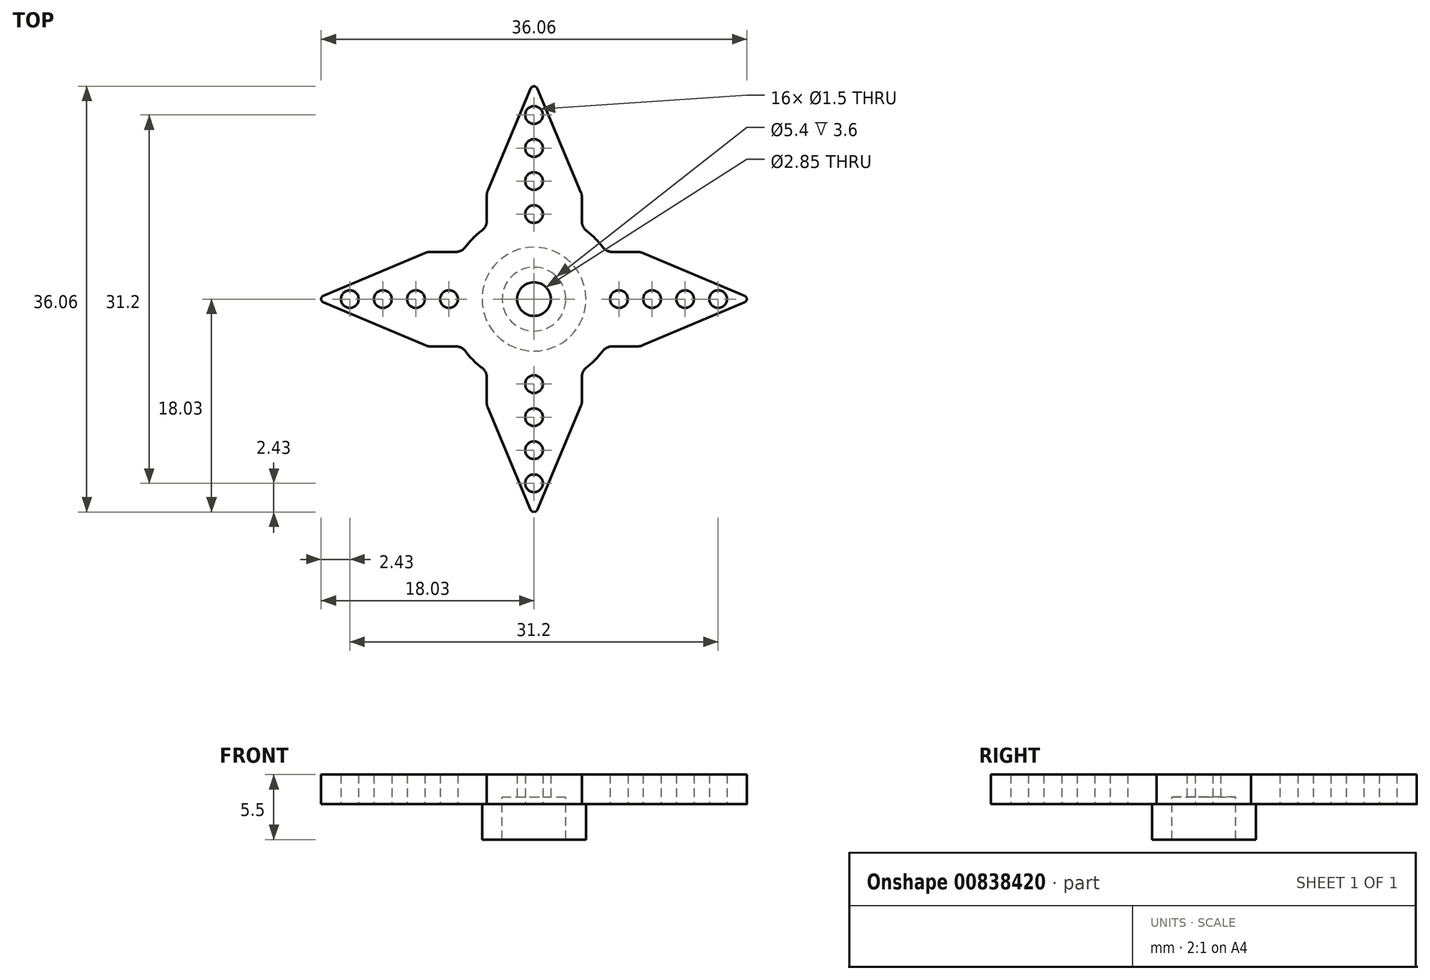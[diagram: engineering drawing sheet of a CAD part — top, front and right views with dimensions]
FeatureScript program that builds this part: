
annotation { "Feature Type Name" : "Feature", "Feature Type Description" : "" }
export const myFeature = defineFeature(function(context is Context, id is Id, definition is map)
    precondition{}
    {
        {
            var Q0;
            Q0=qCreatedBy(makeId("Top.planeOp"),FACE);
            var sketch = newSketch(context, id + "F0", { "sketchPlane" : qUnion([Q0])});
            skCircle(sketch, "E0", {"center": v(0, 0) * mm, "radius": 18.5 * mm, "construction": true});
            skArc(sketch, "E1", {"start": v(5.83, 4.4) * mm, "mid": v(5.18, 5.14) * mm, "end": v(4.45, 5.8) * mm});
            skLineSegment(sketch, "E2", {"start": v(-0.28, 17.84) * mm, "end": v(-3.92, 9.19) * mm});
            skLineSegment(sketch, "E3", {"start": v(-4, 6.62) * mm, "end": v(-4, 8.8) * mm});
            skLineSegment(sketch, "E4", {"start": v(0.28, 17.84) * mm, "end": v(3.98, 9.06) * mm});
            skLineSegment(sketch, "E5", {"start": v(4.05, 8.67) * mm, "end": v(4.05, 6.58) * mm});
            skLineSegment(sketch, "E6.1.0", {"start": v(-8.8, 4) * mm, "end": v(-6.62, 4) * mm});
            skLineSegment(sketch, "E6.1.4", {"start": v(-17.84, 0.28) * mm, "end": v(-9.19, 3.92) * mm});
            skLineSegment(sketch, "E6.3.2", {"start": v(6.62, 4) * mm, "end": v(8.8, 4) * mm});
            skLineSegment(sketch, "E6.3.3", {"start": v(17.84, 0.28) * mm, "end": v(9.19, 3.92) * mm});
            skArc(sketch, "E7.trimOffspring", {"start": v(-4.4, 5.83) * mm, "mid": v(-5.16, 5.16) * mm, "end": v(-5.83, 4.4) * mm});
            skPoint(sketch, "E8.orphan", {"position": v(5, 4) * mm});
            skPoint(sketch, "E9.orphan", {"position": v(4.05, 4.48) * mm});
            skPoint(sketch, "E10.orphan", {"position": v(-4, 5) * mm});
            skPoint(sketch, "E11.orphan", {"position": v(4, -5) * mm});
            skPoint(sketch, "E12.orphan", {"position": v(4.75, -4) * mm});
            skPoint(sketch, "E13.orphan", {"position": v(-4, -4.75) * mm});
            skPoint(sketch, "E14.orphan", {"position": v(-5, -4) * mm});
            skPoint(sketch, "E15.orphan", {"position": v(-4.75, 4) * mm});
            skPoint(sketch, "E16.visualSharp", {"position": v(4.05, 8.87) * mm});
            skArc(sketch, "E16.filletArc", {"start": v(4.05, 8.67) * mm, "mid": v(4.04, 8.87) * mm, "end": v(3.98, 9.06) * mm});
            skPoint(sketch, "E17.visualSharp", {"position": v(-4, 9) * mm});
            skArc(sketch, "E17.filletArc", {"start": v(-3.92, 9.19) * mm, "mid": v(-3.98, 9) * mm, "end": v(-4, 8.8) * mm});
            skPoint(sketch, "E18.visualSharp", {"position": v(4.05, 6.07) * mm});
            skArc(sketch, "E18.filletArc", {"start": v(4.05, 6.58) * mm, "mid": v(4.16, 6.14) * mm, "end": v(4.45, 5.8) * mm});
            skPoint(sketch, "E19.visualSharp", {"position": v(6.1, 4) * mm});
            skArc(sketch, "E19.filletArc", {"start": v(5.83, 4.4) * mm, "mid": v(6.18, 4.1) * mm, "end": v(6.62, 4) * mm});
            skPoint(sketch, "E20.visualSharp", {"position": v(9, 4) * mm});
            skArc(sketch, "E20.filletArc", {"start": v(9.19, 3.92) * mm, "mid": v(9, 3.98) * mm, "end": v(8.8, 4) * mm});
            skPoint(sketch, "E21.visualSharp", {"position": v(-6.1, 4) * mm});
            skArc(sketch, "E21.filletArc", {"start": v(-6.62, 4) * mm, "mid": v(-6.18, 4.1) * mm, "end": v(-5.83, 4.4) * mm});
            skPoint(sketch, "E22.visualSharp", {"position": v(-4, 6.1) * mm});
            skArc(sketch, "E22.filletArc", {"start": v(-4.4, 5.83) * mm, "mid": v(-4.1, 6.18) * mm, "end": v(-4, 6.62) * mm});
            skPoint(sketch, "E23.visualSharp", {"position": v(-9, 4) * mm});
            skArc(sketch, "E23.filletArc", {"start": v(-8.8, 4) * mm, "mid": v(-9, 3.98) * mm, "end": v(-9.19, 3.92) * mm});
            skLineSegment(sketch, "E24.MirrorCS", {"start": v(17.84, -0.28) * mm, "end": v(9.19, -3.92) * mm});
            skArc(sketch, "E25.MirrorCS", {"start": v(-3.92, -9.19) * mm, "mid": v(-3.98, -9) * mm, "end": v(-4, -8.8) * mm});
            skArc(sketch, "E26.MirrorCS", {"start": v(4.05, -8.67) * mm, "mid": v(4.04, -8.87) * mm, "end": v(3.98, -9.06) * mm});
            skArc(sketch, "E27.MirrorCS", {"start": v(-4.4, -5.83) * mm, "mid": v(-4.1, -6.18) * mm, "end": v(-4, -6.62) * mm});
            skLineSegment(sketch, "E28.MirrorCS", {"start": v(4.05, -8.67) * mm, "end": v(4.05, -6.58) * mm});
            skLineSegment(sketch, "E29.MirrorCS", {"start": v(-4, -6.62) * mm, "end": v(-4, -8.8) * mm});
            skArc(sketch, "E30.MirrorCS", {"start": v(-6.62, -4) * mm, "mid": v(-6.18, -4.1) * mm, "end": v(-5.83, -4.4) * mm});
            skArc(sketch, "E31.MirrorCS", {"start": v(4.05, -6.58) * mm, "mid": v(4.16, -6.14) * mm, "end": v(4.45, -5.8) * mm});
            skArc(sketch, "E32.MirrorCS", {"start": v(5.83, -4.4) * mm, "mid": v(5.18, -5.14) * mm, "end": v(4.45, -5.8) * mm});
            skArc(sketch, "E33.MirrorCS", {"start": v(9.19, -3.92) * mm, "mid": v(9, -3.98) * mm, "end": v(8.8, -4) * mm});
            skLineSegment(sketch, "E34.MirrorCS", {"start": v(-8.8, -4) * mm, "end": v(-6.62, -4) * mm});
            skArc(sketch, "E35.MirrorCS", {"start": v(-8.8, -4) * mm, "mid": v(-9, -3.98) * mm, "end": v(-9.19, -3.92) * mm});
            skArc(sketch, "E36.MirrorCS", {"start": v(5.83, -4.4) * mm, "mid": v(6.18, -4.1) * mm, "end": v(6.62, -4) * mm});
            skArc(sketch, "E37.MirrorCS", {"start": v(-4.4, -5.83) * mm, "mid": v(-5.16, -5.16) * mm, "end": v(-5.83, -4.4) * mm});
            skLineSegment(sketch, "E38.MirrorCS", {"start": v(6.62, -4) * mm, "end": v(8.8, -4) * mm});
            skPoint(sketch, "E39.MirrorP", {"position": v(-4, -6.1) * mm});
            skPoint(sketch, "E40.MirrorP", {"position": v(-4.75, -4) * mm});
            skPoint(sketch, "E41.MirrorP", {"position": v(5, -4) * mm});
            skPoint(sketch, "E42.MirrorP", {"position": v(4.05, -8.87) * mm});
            skPoint(sketch, "E43.MirrorP", {"position": v(6.1, -4) * mm});
            skPoint(sketch, "E44.MirrorP", {"position": v(4.05, -6.07) * mm});
            skPoint(sketch, "E45.MirrorP", {"position": v(-6.1, -4) * mm});
            skPoint(sketch, "E46.MirrorP", {"position": v(-9, -4) * mm});
            skPoint(sketch, "E47.MirrorP", {"position": v(4.05, -4.48) * mm});
            skPoint(sketch, "E48.MirrorP", {"position": v(-4, -5) * mm});
            skLineSegment(sketch, "E49.MirrorCS", {"start": v(-17.84, -0.28) * mm, "end": v(-9.19, -3.92) * mm});
            skLineSegment(sketch, "E50.MirrorCS", {"start": v(-0.28, -17.84) * mm, "end": v(-3.92, -9.19) * mm});
            skPoint(sketch, "E51.MirrorP", {"position": v(-4, -9) * mm});
            skLineSegment(sketch, "E52.MirrorCS", {"start": v(0.28, -17.84) * mm, "end": v(3.98, -9.06) * mm});
            skPoint(sketch, "E53.MirrorP", {"position": v(9, -4) * mm});
            skPoint(sketch, "E54.visualSharp", {"position": v(0, 18.5) * mm});
            skArc(sketch, "E54.filletArc", {"start": v(0.28, 17.84) * mm, "mid": v(0, 18.03) * mm, "end": v(-0.28, 17.84) * mm});
            skPoint(sketch, "E55.visualSharp", {"position": v(-18.5, 0) * mm});
            skPoint(sketch, "E56.visualSharp", {"position": v(18.5, 0) * mm});
            skArc(sketch, "E56.filletArc", {"start": v(17.84, -0.28) * mm, "mid": v(18.03, 0) * mm, "end": v(17.84, 0.28) * mm});
            skPoint(sketch, "E57.visualSharp", {"position": v(0, -18.5) * mm});
            skArc(sketch, "E57.filletArc", {"start": v(-0.28, -17.84) * mm, "mid": v(0, -18.03) * mm, "end": v(0.28, -17.84) * mm});
            skArc(sketch, "E58.filletArc", {"start": v(-17.84, 0.28) * mm, "mid": v(-18.03, 0) * mm, "end": v(-17.84, -0.28) * mm});
            skCircle(sketch, "E59", {"center": v(0, 0) * mm, "radius": 7.2 * mm, "construction": true});
            skCircle(sketch, "E60", {"center": v(7.2, 0) * mm, "radius": 0.75 * mm});
            skCircle(sketch, "E61.1.0.0", {"center": v(10, 0) * mm, "radius": 0.75 * mm});
            skCircle(sketch, "E61.2.0.0", {"center": v(12.8, 0) * mm, "radius": 0.75 * mm});
            skCircle(sketch, "E61.3.0.0", {"center": v(15.6, 0) * mm, "radius": 0.75 * mm});
            skLineSegment(sketch, "E61.direction1", {"start": v(7.2, 0) * mm, "end": v(10, 0) * mm, "construction": true});
            skCircle(sketch, "E62.1.0", {"center": v(0, 7.2) * mm, "radius": 0.75 * mm});
            skCircle(sketch, "E62.1.1", {"center": v(0, 12.8) * mm, "radius": 0.75 * mm});
            skCircle(sketch, "E62.1.2", {"center": v(0, 15.6) * mm, "radius": 0.75 * mm});
            skCircle(sketch, "E62.1.3", {"center": v(0, 10) * mm, "radius": 0.75 * mm});
            skCircle(sketch, "E62.2.0", {"center": v(-7.2, 0) * mm, "radius": 0.75 * mm});
            skCircle(sketch, "E62.2.1", {"center": v(-12.8, 0) * mm, "radius": 0.75 * mm});
            skCircle(sketch, "E62.2.2", {"center": v(-15.6, 0) * mm, "radius": 0.75 * mm});
            skCircle(sketch, "E62.2.3", {"center": v(-10, 0) * mm, "radius": 0.75 * mm});
            skCircle(sketch, "E62.3.0", {"center": v(0, -7.2) * mm, "radius": 0.75 * mm});
            skCircle(sketch, "E62.3.1", {"center": v(0, -12.8) * mm, "radius": 0.75 * mm});
            skCircle(sketch, "E62.3.2", {"center": v(0, -15.6) * mm, "radius": 0.75 * mm});
            skCircle(sketch, "E62.3.3", {"center": v(0, -10) * mm, "radius": 0.75 * mm});
            skSolve(sketch);
        }
        {
            var Q0;
            Q0 = qSketchRegion(id + "F0", true);
            extrude(context, id + "F1", {"entities" : qUnion([Q0]), "depth" : 2.5 * mm, "offsetDistance" : 25 * mm});
        }
        {
            var Q0;
            Q0=makeQuery(id+"F1.opExtrude","CAP_FACE",FACE,{"disambiguationData":[OSD([sQuery(id+"F0.wireOp",EDGE,"E1"),sQuery(id+"F0.wireOp",EDGE,"E2"),sQuery(id+"F0.wireOp",EDGE,"E3"),sQuery(id+"F0.wireOp",EDGE,"E4"),sQuery(id+"F0.wireOp",EDGE,"E5"),sQuery(id+"F0.wireOp",EDGE,"E6.1.0"),sQuery(id+"F0.wireOp",EDGE,"E6.1.4"),sQuery(id+"F0.wireOp",EDGE,"E6.3.2"),sQuery(id+"F0.wireOp",EDGE,"E6.3.3"),sQuery(id+"F0.wireOp",EDGE,"E7.trimOffspring"),sQuery(id+"F0.wireOp",EDGE,"E16.filletArc"),sQuery(id+"F0.wireOp",EDGE,"E18.filletArc"),sQuery(id+"F0.wireOp",EDGE,"E19.filletArc"),sQuery(id+"F0.wireOp",EDGE,"E20.filletArc"),sQuery(id+"F0.wireOp",EDGE,"E21.filletArc"),sQuery(id+"F0.wireOp",EDGE,"E22.filletArc"),sQuery(id+"F0.wireOp",EDGE,"E17.filletArc"),sQuery(id+"F0.wireOp",EDGE,"E23.filletArc"),sQuery(id+"F0.wireOp",EDGE,"E24.MirrorCS"),sQuery(id+"F0.wireOp",EDGE,"E26.MirrorCS"),sQuery(id+"F0.wireOp",EDGE,"E25.MirrorCS"),sQuery(id+"F0.wireOp",EDGE,"E27.MirrorCS"),sQuery(id+"F0.wireOp",EDGE,"E28.MirrorCS"),sQuery(id+"F0.wireOp",EDGE,"E29.MirrorCS"),sQuery(id+"F0.wireOp",EDGE,"E30.MirrorCS"),sQuery(id+"F0.wireOp",EDGE,"E31.MirrorCS"),sQuery(id+"F0.wireOp",EDGE,"E32.MirrorCS"),sQuery(id+"F0.wireOp",EDGE,"E33.MirrorCS"),sQuery(id+"F0.wireOp",EDGE,"E34.MirrorCS"),sQuery(id+"F0.wireOp",EDGE,"E35.MirrorCS"),sQuery(id+"F0.wireOp",EDGE,"E36.MirrorCS"),sQuery(id+"F0.wireOp",EDGE,"E37.MirrorCS"),sQuery(id+"F0.wireOp",EDGE,"E38.MirrorCS"),sQuery(id+"F0.wireOp",EDGE,"E49.MirrorCS"),sQuery(id+"F0.wireOp",EDGE,"E50.MirrorCS"),sQuery(id+"F0.wireOp",EDGE,"E52.MirrorCS"),sQuery(id+"F0.wireOp",EDGE,"E54.filletArc"),sQuery(id+"F0.wireOp",EDGE,"E56.filletArc"),sQuery(id+"F0.wireOp",EDGE,"E57.filletArc"),sQuery(id+"F0.wireOp",EDGE,"E58.filletArc"),sQuery(id+"F0.wireOp",EDGE,"E60"),sQuery(id+"F0.wireOp",EDGE,"E61.1.0.0"),sQuery(id+"F0.wireOp",EDGE,"E61.2.0.0"),sQuery(id+"F0.wireOp",EDGE,"E61.3.0.0"),sQuery(id+"F0.wireOp",EDGE,"E62.1.0"),sQuery(id+"F0.wireOp",EDGE,"E62.1.1"),sQuery(id+"F0.wireOp",EDGE,"E62.1.2"),sQuery(id+"F0.wireOp",EDGE,"E62.1.3"),sQuery(id+"F0.wireOp",EDGE,"E62.2.0"),sQuery(id+"F0.wireOp",EDGE,"E62.2.1"),sQuery(id+"F0.wireOp",EDGE,"E62.2.2"),sQuery(id+"F0.wireOp",EDGE,"E62.2.3"),sQuery(id+"F0.wireOp",EDGE,"E62.3.0"),sQuery(id+"F0.wireOp",EDGE,"E62.3.1"),sQuery(id+"F0.wireOp",EDGE,"E62.3.2"),sQuery(id+"F0.wireOp",EDGE,"E62.3.3")])],"isStart":true});
            var sketch = newSketch(context, id + "F2", { "sketchPlane" : qUnion([Q0])});
            skCircle(sketch, "E63", {"center": v(0, 0) * mm, "radius": 4.4 * mm});
            skCircle(sketch, "E64", {"center": v(0, 0) * mm, "radius": 2.7 * mm});
            skSolve(sketch);
        }
        {
            var Q0;
            Q0=makeQuery(id+"F2.imprint","IMPRINT",FACE,{"disambiguationData":[TD([[makeQuery(id+"F2.imprint","IMPRINT",EDGE,{"derivedFrom":sQuery(id+"F2.wireOp",EDGE,"E63")}),1.0]])]});
            var Q1;
            Q1=sQuery(id+"F2.wireOp",EDGE,"E63");
            var Q2;
            Q2=sQuery(id+"F2.wireOp",EDGE,"E64");
            extrude(context, id + "F3", {"entities" : qUnion([Q0]), "operationType" : NewBodyOperationType.ADD, "surfaceEntities" : qUnion([Q1, Q2]), "depth" : 3 * mm, "offsetDistance" : 25 * mm});
        }
        {
            var Q0;
            Q0=makeQuery(id+"F3.boolean.opBoolean","SPLIT",FACE,{"disambiguationData":[TD([makeQuery(id+"F3.opExtrude","SWEPT_FACE",FACE,{"disambiguationData":[OSD([sQuery(id+"F2.wireOp",EDGE,"E64")])]})])],"derivedFrom":makeQuery(id+"F1.opExtrude","CAP_FACE",FACE,{"disambiguationData":[OSD([sQuery(id+"F0.wireOp",EDGE,"E1"),sQuery(id+"F0.wireOp",EDGE,"E2"),sQuery(id+"F0.wireOp",EDGE,"E3"),sQuery(id+"F0.wireOp",EDGE,"E4"),sQuery(id+"F0.wireOp",EDGE,"E5"),sQuery(id+"F0.wireOp",EDGE,"E6.1.0"),sQuery(id+"F0.wireOp",EDGE,"E6.1.4"),sQuery(id+"F0.wireOp",EDGE,"E6.3.2"),sQuery(id+"F0.wireOp",EDGE,"E6.3.3"),sQuery(id+"F0.wireOp",EDGE,"E7.trimOffspring"),sQuery(id+"F0.wireOp",EDGE,"E16.filletArc"),sQuery(id+"F0.wireOp",EDGE,"E18.filletArc"),sQuery(id+"F0.wireOp",EDGE,"E19.filletArc"),sQuery(id+"F0.wireOp",EDGE,"E20.filletArc"),sQuery(id+"F0.wireOp",EDGE,"E21.filletArc"),sQuery(id+"F0.wireOp",EDGE,"E22.filletArc"),sQuery(id+"F0.wireOp",EDGE,"E17.filletArc"),sQuery(id+"F0.wireOp",EDGE,"E23.filletArc"),sQuery(id+"F0.wireOp",EDGE,"E24.MirrorCS"),sQuery(id+"F0.wireOp",EDGE,"E26.MirrorCS"),sQuery(id+"F0.wireOp",EDGE,"E25.MirrorCS"),sQuery(id+"F0.wireOp",EDGE,"E27.MirrorCS"),sQuery(id+"F0.wireOp",EDGE,"E28.MirrorCS"),sQuery(id+"F0.wireOp",EDGE,"E29.MirrorCS"),sQuery(id+"F0.wireOp",EDGE,"E30.MirrorCS"),sQuery(id+"F0.wireOp",EDGE,"E31.MirrorCS"),sQuery(id+"F0.wireOp",EDGE,"E32.MirrorCS"),sQuery(id+"F0.wireOp",EDGE,"E33.MirrorCS"),sQuery(id+"F0.wireOp",EDGE,"E34.MirrorCS"),sQuery(id+"F0.wireOp",EDGE,"E35.MirrorCS"),sQuery(id+"F0.wireOp",EDGE,"E36.MirrorCS"),sQuery(id+"F0.wireOp",EDGE,"E37.MirrorCS"),sQuery(id+"F0.wireOp",EDGE,"E38.MirrorCS"),sQuery(id+"F0.wireOp",EDGE,"E49.MirrorCS"),sQuery(id+"F0.wireOp",EDGE,"E50.MirrorCS"),sQuery(id+"F0.wireOp",EDGE,"E52.MirrorCS"),sQuery(id+"F0.wireOp",EDGE,"E54.filletArc"),sQuery(id+"F0.wireOp",EDGE,"E56.filletArc"),sQuery(id+"F0.wireOp",EDGE,"E57.filletArc"),sQuery(id+"F0.wireOp",EDGE,"E58.filletArc"),sQuery(id+"F0.wireOp",EDGE,"E60"),sQuery(id+"F0.wireOp",EDGE,"E61.1.0.0"),sQuery(id+"F0.wireOp",EDGE,"E61.2.0.0"),sQuery(id+"F0.wireOp",EDGE,"E61.3.0.0"),sQuery(id+"F0.wireOp",EDGE,"E62.1.0"),sQuery(id+"F0.wireOp",EDGE,"E62.1.1"),sQuery(id+"F0.wireOp",EDGE,"E62.1.2"),sQuery(id+"F0.wireOp",EDGE,"E62.1.3"),sQuery(id+"F0.wireOp",EDGE,"E62.2.0"),sQuery(id+"F0.wireOp",EDGE,"E62.2.1"),sQuery(id+"F0.wireOp",EDGE,"E62.2.2"),sQuery(id+"F0.wireOp",EDGE,"E62.2.3"),sQuery(id+"F0.wireOp",EDGE,"E62.3.0"),sQuery(id+"F0.wireOp",EDGE,"E62.3.1"),sQuery(id+"F0.wireOp",EDGE,"E62.3.2"),sQuery(id+"F0.wireOp",EDGE,"E62.3.3")])],"isStart":true})});
            var sketch = newSketch(context, id + "F4", { "sketchPlane" : qUnion([Q0])});
            skCircle(sketch, "E65", {"center": v(0, 0) * mm, "radius": 1.43 * mm});
            skSolve(sketch);
        }
        {
            var Q0;
            Q0=makeQuery(id+"F4.imprint","IMPRINT",FACE,{"disambiguationData":[TD([[makeQuery(id+"F4.imprint","IMPRINT",EDGE,{"derivedFrom":sQuery(id+"F4.wireOp",EDGE,"E65")}),1.0]])]});
            var Q1;
            Q1=sQuery(id+"F4.wireOp",EDGE,"E65");
            extrude(context, id + "F5", {"entities" : qUnion([Q0]), "operationType" : NewBodyOperationType.REMOVE, "surfaceEntities" : qUnion([Q1]), "oppositeDirection" : true, "depth" : 25 * mm, "offsetDistance" : 25 * mm});
        }
        {
            var Q0;
            Q0=makeQuery(id+"F3.boolean.opBoolean","SPLIT",FACE,{"disambiguationData":[TD([makeQuery(id+"F3.opExtrude","SWEPT_FACE",FACE,{"disambiguationData":[OSD([sQuery(id+"F2.wireOp",EDGE,"E64")])]})])],"derivedFrom":makeQuery(id+"F1.opExtrude","CAP_FACE",FACE,{"disambiguationData":[OSD([sQuery(id+"F0.wireOp",EDGE,"E1"),sQuery(id+"F0.wireOp",EDGE,"E2"),sQuery(id+"F0.wireOp",EDGE,"E3"),sQuery(id+"F0.wireOp",EDGE,"E4"),sQuery(id+"F0.wireOp",EDGE,"E5"),sQuery(id+"F0.wireOp",EDGE,"E6.1.0"),sQuery(id+"F0.wireOp",EDGE,"E6.1.4"),sQuery(id+"F0.wireOp",EDGE,"E6.3.2"),sQuery(id+"F0.wireOp",EDGE,"E6.3.3"),sQuery(id+"F0.wireOp",EDGE,"E7.trimOffspring"),sQuery(id+"F0.wireOp",EDGE,"E16.filletArc"),sQuery(id+"F0.wireOp",EDGE,"E18.filletArc"),sQuery(id+"F0.wireOp",EDGE,"E19.filletArc"),sQuery(id+"F0.wireOp",EDGE,"E20.filletArc"),sQuery(id+"F0.wireOp",EDGE,"E21.filletArc"),sQuery(id+"F0.wireOp",EDGE,"E22.filletArc"),sQuery(id+"F0.wireOp",EDGE,"E17.filletArc"),sQuery(id+"F0.wireOp",EDGE,"E23.filletArc"),sQuery(id+"F0.wireOp",EDGE,"E24.MirrorCS"),sQuery(id+"F0.wireOp",EDGE,"E26.MirrorCS"),sQuery(id+"F0.wireOp",EDGE,"E25.MirrorCS"),sQuery(id+"F0.wireOp",EDGE,"E27.MirrorCS"),sQuery(id+"F0.wireOp",EDGE,"E28.MirrorCS"),sQuery(id+"F0.wireOp",EDGE,"E29.MirrorCS"),sQuery(id+"F0.wireOp",EDGE,"E30.MirrorCS"),sQuery(id+"F0.wireOp",EDGE,"E31.MirrorCS"),sQuery(id+"F0.wireOp",EDGE,"E32.MirrorCS"),sQuery(id+"F0.wireOp",EDGE,"E33.MirrorCS"),sQuery(id+"F0.wireOp",EDGE,"E34.MirrorCS"),sQuery(id+"F0.wireOp",EDGE,"E35.MirrorCS"),sQuery(id+"F0.wireOp",EDGE,"E36.MirrorCS"),sQuery(id+"F0.wireOp",EDGE,"E37.MirrorCS"),sQuery(id+"F0.wireOp",EDGE,"E38.MirrorCS"),sQuery(id+"F0.wireOp",EDGE,"E49.MirrorCS"),sQuery(id+"F0.wireOp",EDGE,"E50.MirrorCS"),sQuery(id+"F0.wireOp",EDGE,"E52.MirrorCS"),sQuery(id+"F0.wireOp",EDGE,"E54.filletArc"),sQuery(id+"F0.wireOp",EDGE,"E56.filletArc"),sQuery(id+"F0.wireOp",EDGE,"E57.filletArc"),sQuery(id+"F0.wireOp",EDGE,"E58.filletArc"),sQuery(id+"F0.wireOp",EDGE,"E60"),sQuery(id+"F0.wireOp",EDGE,"E61.1.0.0"),sQuery(id+"F0.wireOp",EDGE,"E61.2.0.0"),sQuery(id+"F0.wireOp",EDGE,"E61.3.0.0"),sQuery(id+"F0.wireOp",EDGE,"E62.1.0"),sQuery(id+"F0.wireOp",EDGE,"E62.1.1"),sQuery(id+"F0.wireOp",EDGE,"E62.1.2"),sQuery(id+"F0.wireOp",EDGE,"E62.1.3"),sQuery(id+"F0.wireOp",EDGE,"E62.2.0"),sQuery(id+"F0.wireOp",EDGE,"E62.2.1"),sQuery(id+"F0.wireOp",EDGE,"E62.2.2"),sQuery(id+"F0.wireOp",EDGE,"E62.2.3"),sQuery(id+"F0.wireOp",EDGE,"E62.3.0"),sQuery(id+"F0.wireOp",EDGE,"E62.3.1"),sQuery(id+"F0.wireOp",EDGE,"E62.3.2"),sQuery(id+"F0.wireOp",EDGE,"E62.3.3")])],"isStart":true})});
            extrude(context, id + "F6", {"entities" : qUnion([Q0]), "operationType" : NewBodyOperationType.REMOVE, "oppositeDirection" : true, "depth" : 0.6 * mm, "offsetDistance" : 25 * mm});
        }
    });
